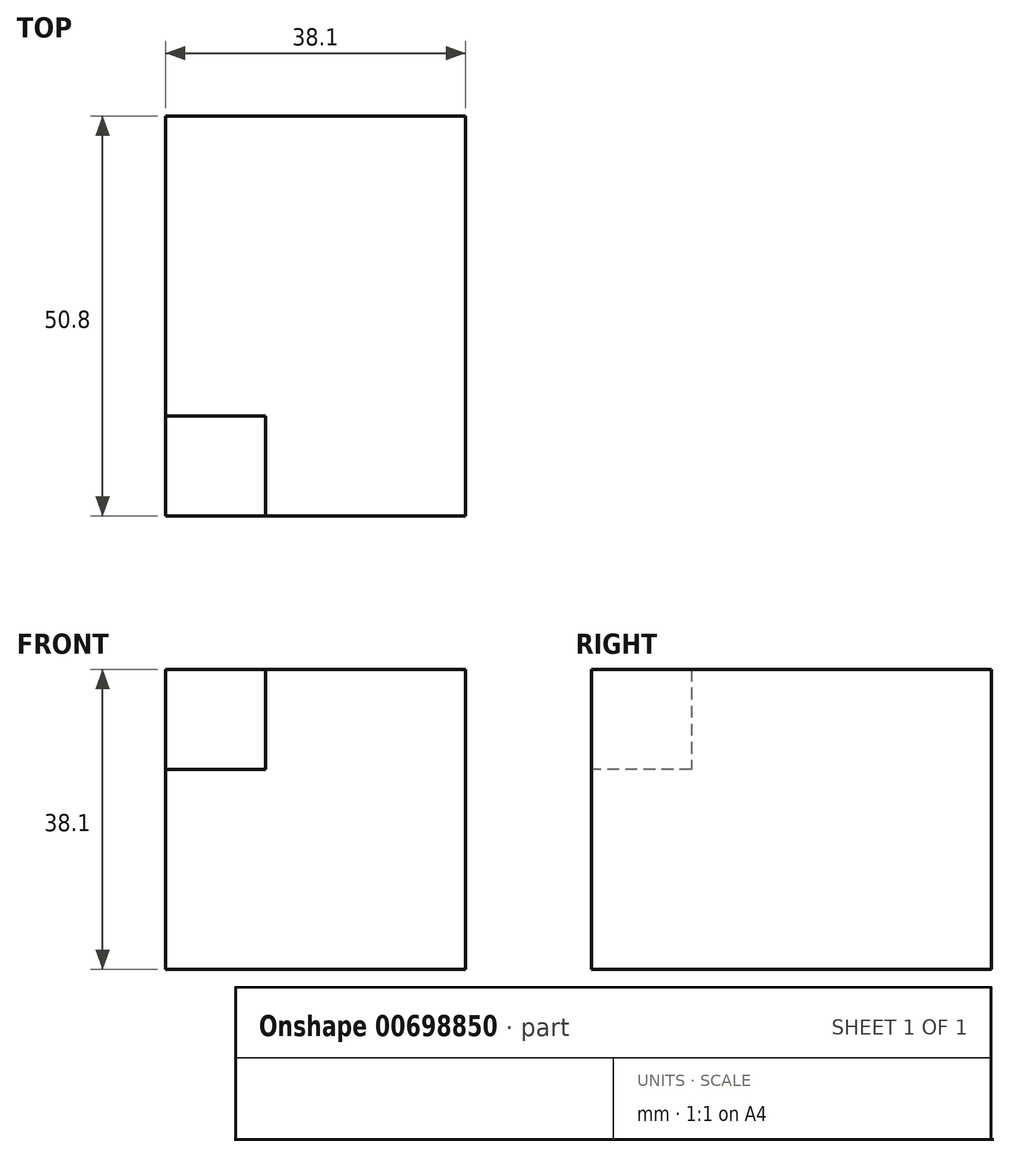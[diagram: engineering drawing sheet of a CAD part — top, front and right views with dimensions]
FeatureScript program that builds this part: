
annotation { "Feature Type Name" : "Feature", "Feature Type Description" : "" }
export const myFeature = defineFeature(function(context is Context, id is Id, definition is map)
    precondition{}
    {
        {
            var Q0;
            Q0=qCreatedBy(makeId("Front.planeOp"),FACE);
            var sketch = newSketch(context, id + "F0", { "sketchPlane" : qUnion([Q0])});
            skLineSegment(sketch, "E0", {"start": v(0, 0) * mm, "end": v(0, 38.1) * mm});
            skLineSegment(sketch, "E1", {"start": v(0, 38.1) * mm, "end": v(-38.1, 38.1) * mm});
            skLineSegment(sketch, "E2", {"start": v(-38.1, 38.1) * mm, "end": v(-38.1, 0) * mm});
            skLineSegment(sketch, "E3", {"start": v(-38.1, 0) * mm, "end": v(0, 0) * mm});
            skSolve(sketch);
        }
        {
            var Q0;
            Q0=makeQuery(id+"F0.imprint","IMPRINT",FACE,{"disambiguationData":[TD([[makeQuery(id+"F0.imprint","IMPRINT",EDGE,{"derivedFrom":sQuery(id+"F0.wireOp",EDGE,"E0")}),1.0]])]});
            extrude(context, id + "F1", {"entities" : qUnion([Q0]), "depth" : 50.8 * mm, "offsetDistance" : 25.4 * mm});
        }
        {
            var Q0;
            Q0=makeQuery(id+"F1.opExtrude","CAP_FACE",FACE,{"disambiguationData":[OSD([sQuery(id+"F0.wireOp",EDGE,"E0"),sQuery(id+"F0.wireOp",EDGE,"E1"),sQuery(id+"F0.wireOp",EDGE,"E2"),sQuery(id+"F0.wireOp",EDGE,"E3")])],"isStart":false});
            var sketch = newSketch(context, id + "F2", { "sketchPlane" : qUnion([Q0])});
            skLineSegment(sketch, "E4.bottom", {"start": v(-38.1, 38.1) * mm, "end": v(-25.4, 38.1) * mm});
            skLineSegment(sketch, "E4.top", {"start": v(-38.1, 25.4) * mm, "end": v(-25.4, 25.4) * mm});
            skLineSegment(sketch, "E4.left", {"start": v(-38.1, 38.1) * mm, "end": v(-38.1, 25.4) * mm});
            skLineSegment(sketch, "E4.right", {"start": v(-25.4, 38.1) * mm, "end": v(-25.4, 25.4) * mm});
            skSolve(sketch);
        }
        {
            var Q0;
            Q0=makeQuery(id+"F2.imprint","IMPRINT",FACE,{"disambiguationData":[TD([[makeQuery(id+"F2.imprint","IMPRINT",EDGE,{"derivedFrom":sQuery(id+"F2.wireOp",EDGE,"E4.bottom")}),1.0]])]});
            extrude(context, id + "F3", {"entities" : qUnion([Q0]), "operationType" : NewBodyOperationType.REMOVE, "oppositeDirection" : true, "depth" : 12.7 * mm, "offsetDistance" : 25.4 * mm});
        }
    });
